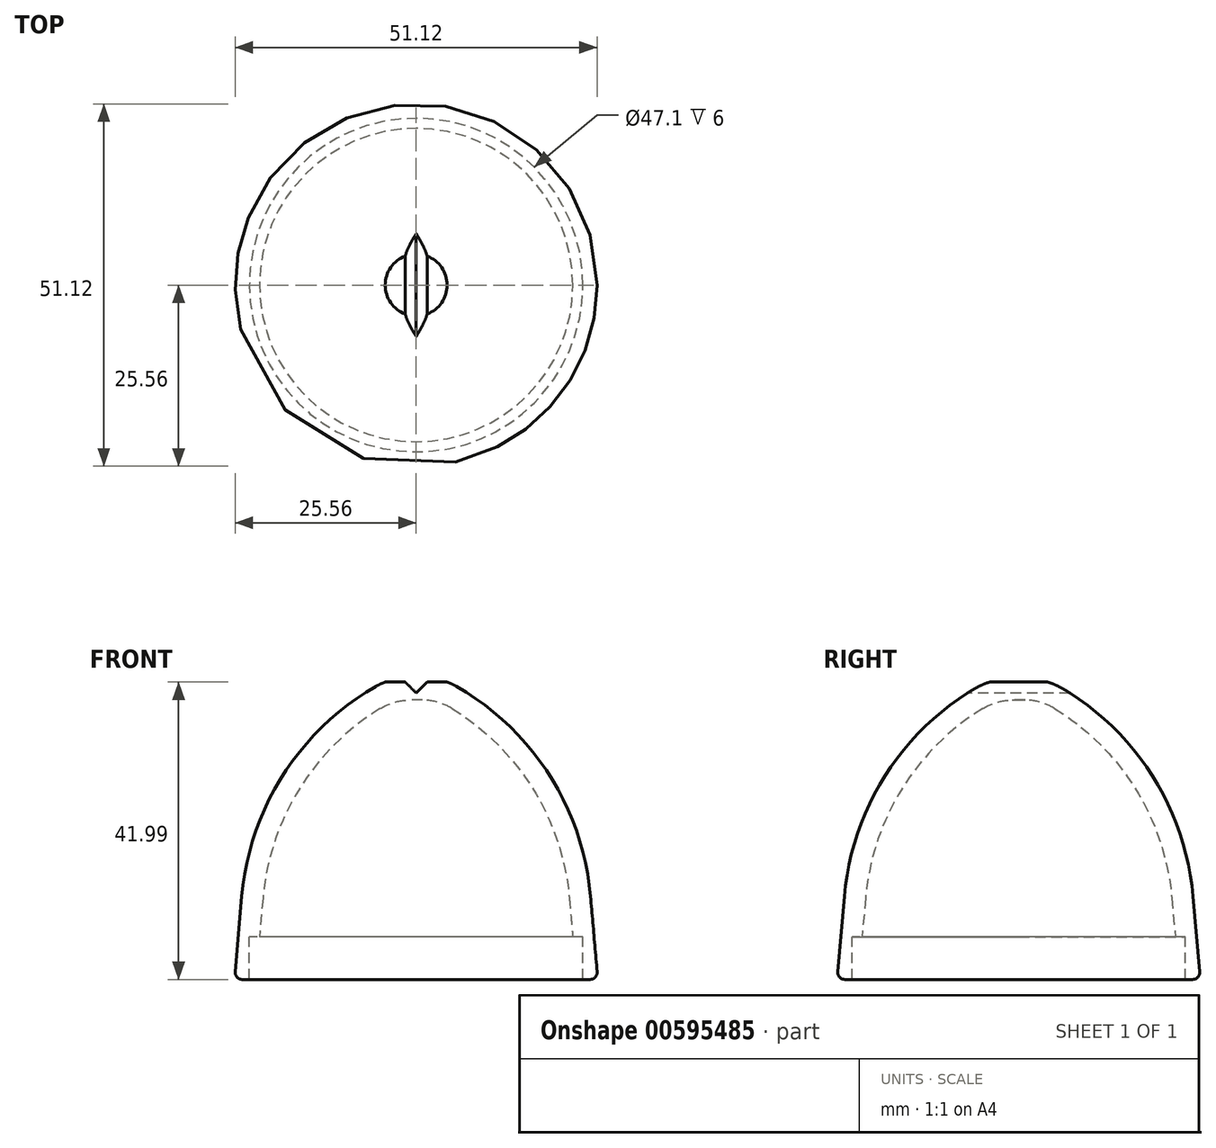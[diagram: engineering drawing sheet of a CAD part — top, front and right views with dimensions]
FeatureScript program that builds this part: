
annotation { "Feature Type Name" : "Feature", "Feature Type Description" : "" }
export const myFeature = defineFeature(function(context is Context, id is Id, definition is map)
    precondition{}
    {
        {
            var Q0;
            Q0=qCreatedBy(makeId("Front.planeOp"),FACE);
            var sketch = newSketch(context, id + "F0", { "sketchPlane" : qUnion([Q0])});
            skLineSegment(sketch, "E0", {"start": v(21.64, 8.05) * mm, "end": v(22.12, 2.57) * mm});
            skArc(sketch, "E1", {"start": v(21.64, 8.05) * mm, "mid": v(16.54, 23.4) * mm, "end": v(5.08, 34.83) * mm});
            skLineSegment(sketch, "E2.0", {"start": v(24.63, 8.31) * mm, "end": v(25.56, -2.34) * mm});
            skArc(sketch, "E2.1", {"start": v(24.63, 8.31) * mm, "mid": v(18.8, 25.45) * mm, "end": v(5.7, 37.95) * mm});
            skLineSegment(sketch, "E3", {"start": v(23.55, -3.43) * mm, "end": v(23.55, 2.57) * mm});
            skPoint(sketch, "E4.orphan", {"position": v(25.65, -3.43) * mm});
            skLineSegment(sketch, "E5", {"start": v(23.55, -3.43) * mm, "end": v(24.56, -3.43) * mm});
            skLineSegment(sketch, "E6", {"start": v(23.55, 2.57) * mm, "end": v(22.12, 2.57) * mm});
            skLineSegment(sketch, "E7", {"start": v(0, 39.01) * mm, "end": v(1.71, 39.01) * mm});
            skPoint(sketch, "E8.orphan", {"position": v(0, 40.62) * mm});
            skLineSegment(sketch, "E9.0", {"start": v(0, 36.01) * mm, "end": v(0.9, 36.01) * mm});
            skPoint(sketch, "E10.visualSharp", {"position": v(3, 36.01) * mm});
            skArc(sketch, "E10.filletArc", {"start": v(5.08, 34.83) * mm, "mid": v(3.07, 35.71) * mm, "end": v(0.9, 36.01) * mm});
            skPoint(sketch, "E11.visualSharp", {"position": v(3.72, 39.01) * mm});
            skArc(sketch, "E11.filletArc", {"start": v(5.7, 37.95) * mm, "mid": v(3.78, 38.74) * mm, "end": v(1.71, 39.01) * mm});
            skLineSegment(sketch, "E12", {"start": v(0, 39.01) * mm, "end": v(0, 36.01) * mm});
            skArc(sketch, "E13.filletArc", {"start": v(24.56, -3.43) * mm, "mid": v(25.3, -3.1) * mm, "end": v(25.56, -2.34) * mm});
            skSolve(sketch);
        }
        {
            var Q0;
            Q0=makeQuery(id+"F0.imprint","IMPRINT",FACE,{"disambiguationData":[TD([[makeQuery(id+"F0.imprint","IMPRINT",EDGE,{"derivedFrom":sQuery(id+"F0.wireOp",EDGE,"E0")}),1.0]])]});
            var Q1;
            Q1=sQuery(id+"F0.wireOp",EDGE,"E12");
            revolve(context, id + "F1", {"entities" : qUnion([Q0]), "axis" : qUnion([Q1]), "revolveType" : RevolveType.FULL});
        }
        {
            var Q0;
            Q0=qCreatedBy(makeId("Front.planeOp"),FACE);
            var sketch = newSketch(context, id + "F2", { "sketchPlane" : qUnion([Q0])});
            skLineSegment(sketch, "E14", {"start": v(-1.55, 38.56) * mm, "end": v(0, 37.01) * mm});
            skLineSegment(sketch, "E15", {"start": v(-1.55, 38.56) * mm, "end": v(-9.07, 38.56) * mm});
            skLineSegment(sketch, "E16", {"start": v(-9.07, 38.56) * mm, "end": v(-9.07, 40.63) * mm});
            skLineSegment(sketch, "E17", {"start": v(-9.07, 40.63) * mm, "end": v(-3.62, 40.63) * mm});
            skPoint(sketch, "E18.MirrorCS.end.orphan", {"position": v(0, 37.01) * mm});
            skLineSegment(sketch, "E19.MirrorCS", {"start": v(1.55, 38.56) * mm, "end": v(0, 37.01) * mm});
            skLineSegment(sketch, "E20.MirrorCS", {"start": v(1.55, 38.56) * mm, "end": v(9.07, 38.56) * mm});
            skLineSegment(sketch, "E21.MirrorCS", {"start": v(9.07, 38.56) * mm, "end": v(9.07, 40.63) * mm});
            skLineSegment(sketch, "E22.MirrorCS", {"start": v(9.07, 40.63) * mm, "end": v(3.62, 40.63) * mm});
            skLineSegment(sketch, "E23", {"start": v(-3.62, 40.63) * mm, "end": v(3.62, 40.63) * mm});
            skSolve(sketch);
        }
        {
            var Q0;
            Q0=makeQuery(id+"F2.imprint","IMPRINT",FACE,{"disambiguationData":[TD([[makeQuery(id+"F2.imprint","IMPRINT",EDGE,{"derivedFrom":sQuery(id+"F2.wireOp",EDGE,"E14")}),1.0]])]});
            extrude(context, id + "F3", {"entities" : qUnion([Q0]), "operationType" : NewBodyOperationType.REMOVE, "endBound" : BoundingType.SYMMETRIC, "oppositeDirection" : true, "depth" : 25 * mm, "offsetDistance" : 25 * mm});
        }
    });
